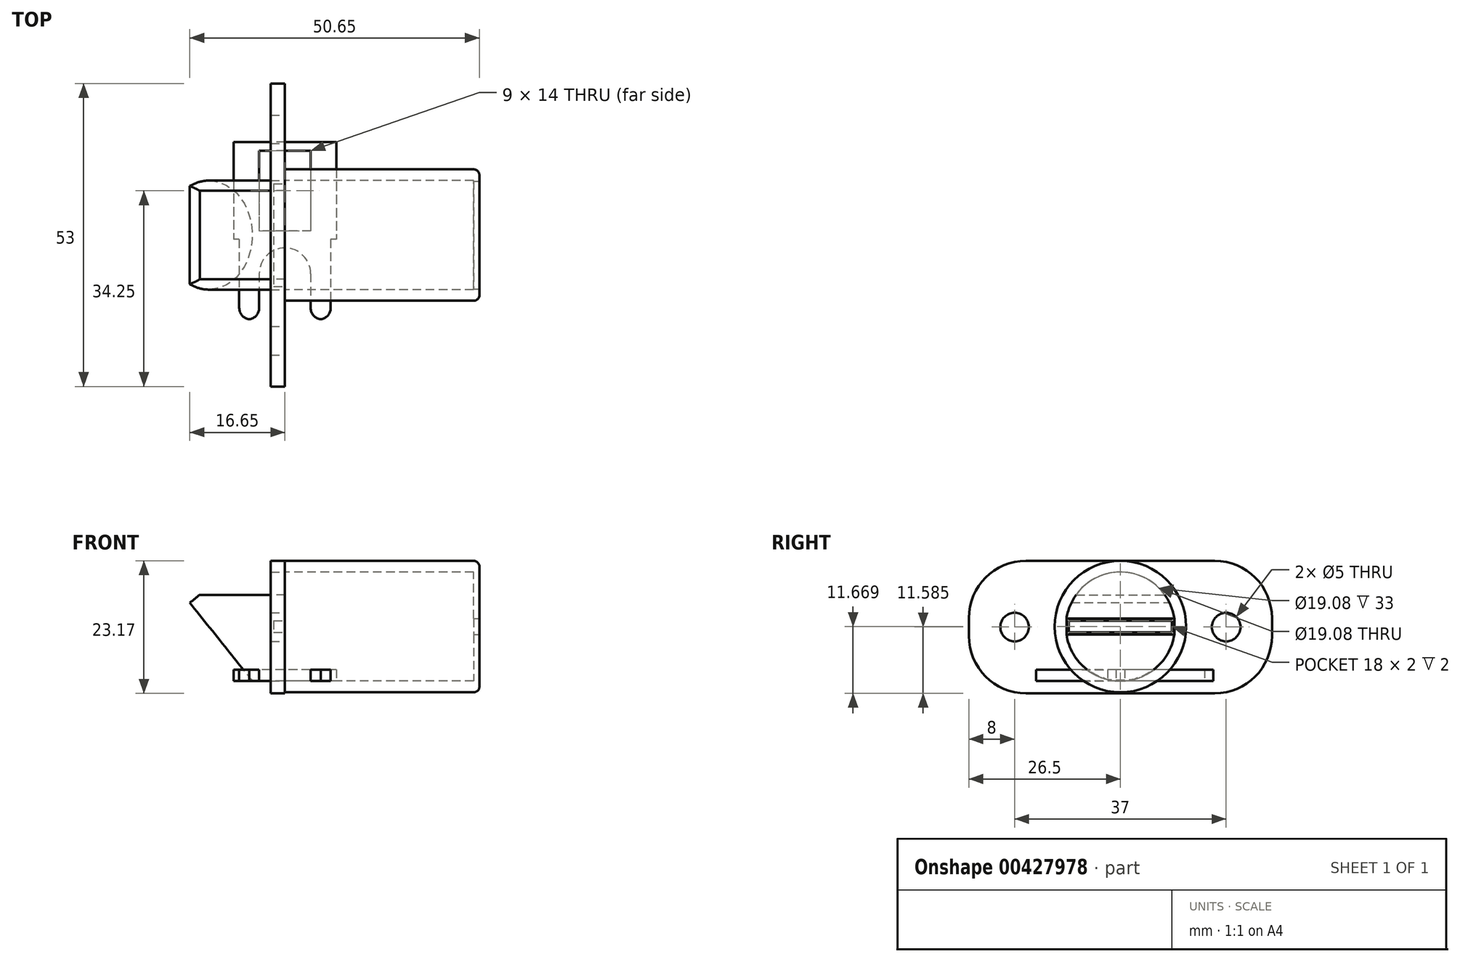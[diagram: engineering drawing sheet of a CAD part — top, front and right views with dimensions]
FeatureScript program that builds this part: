
annotation { "Feature Type Name" : "Feature", "Feature Type Description" : "" }
export const myFeature = defineFeature(function(context is Context, id is Id, definition is map)
    precondition{}
    {
        {
            var Q0;
            Q0=qCreatedBy(makeId("Front.planeOp"),FACE);
            var sketch = newSketch(context, id + "F0", { "sketchPlane" : qUnion([Q0])});
            skLineSegment(sketch, "E0", {"start": v(0, 0) * mm, "end": v(0, 15.1) * mm});
            skLineSegment(sketch, "E1", {"start": v(0, 15.1) * mm, "end": v(-14.9, 15.1) * mm});
            skLineSegment(sketch, "E2", {"start": v(0, 0) * mm, "end": v(-5.67, 0) * mm});
            skLineSegment(sketch, "E3", {"start": v(-5.67, 0) * mm, "end": v(-16.65, 13.71) * mm});
            skLineSegment(sketch, "E4", {"start": v(-16.65, 13.71) * mm, "end": v(-14.9, 15.1) * mm});
            skSolve(sketch);
        }
        {
            var Q0;
            Q0 = qSketchRegion(id + "F0", true);
            extrude(context, id + "F1", {"entities" : qUnion([Q0]), "depth" : 15.5 * mm});
        }
        {
            var Q0;
            Q0=makeQuery(id+"F1.opExtrude","SWEPT_FACE",FACE,{"disambiguationData":[OSD([sQuery(id+"F0.wireOp",EDGE,"E0")])]});
            var sketch = newSketch(context, id + "F2", { "sketchPlane" : qUnion([Q0])});
            skCircle(sketch, "E5", {"center": v(-7.75, 9.54) * mm, "radius": 9.54 * mm});
            skSolve(sketch);
        }
        {
            var Q0;
            {var subQ0=sQuery(id+"F2.wireOp",EDGE,"E5");var subQ1=sQuery(id+"F0.wireOp",EDGE,"E0");var subQ2=makeQuery(id+"F1.opExtrude","CAP_EDGE",EDGE,{"disambiguationData":[OSD([subQ1])],"isStart":false});var subQ4=makeQuery(id+"F2.imprint","INTERSECT",VERTEX,{"derivedFrom":[subQ2,subQ0]});Q0=makeQuery(id+"F2.imprint","IMPRINT",FACE,{"disambiguationData":[TD([[makeQuery(id+"F2.imprint","IMPRINT",EDGE,{"disambiguationData":[TD([[subQ4,1.0]])],"derivedFrom":subQ0}),1.0]])]});}
            var Q1;
            {var subQ0=sQuery(id+"F2.wireOp",EDGE,"E5");var subQ1=sQuery(id+"F0.wireOp",EDGE,"E0");var subQ2=makeQuery(id+"F1.opExtrude","CAP_EDGE",EDGE,{"disambiguationData":[OSD([subQ1])],"isStart":true});var subQ4=makeQuery(id+"F2.imprint","INTERSECT",VERTEX,{"derivedFrom":[subQ2,subQ0]});Q1=makeQuery(id+"F2.imprint","IMPRINT",FACE,{"disambiguationData":[TD([[makeQuery(id+"F2.imprint","IMPRINT",EDGE,{"disambiguationData":[TD([[subQ4,-1.0]])],"derivedFrom":subQ0}),1.0]])]});}
            extrude(context, id + "F3", {"entities" : qUnion([Q0, Q1]), "operationType" : NewBodyOperationType.ADD, "oppositeDirection" : true, "depth" : 16.67 * mm});
        }
        {
            var Q0;
            {var subQ0=sQuery(id+"F2.wireOp",EDGE,"E5");var subQ1=sQuery(id+"F0.wireOp",EDGE,"E0");var subQ2=makeQuery(id+"F1.opExtrude","CAP_EDGE",EDGE,{"disambiguationData":[OSD([subQ1])],"isStart":false});Q0=makeQuery(id+"F3.opExtrude","SWEPT_FACE",FACE,{"disambiguationData":[OSD([subQ1]),TDD([makeQuery(id+"F2.imprint","IMPRINT",EDGE,{"disambiguationData":[TD([[makeQuery(id+"F2.imprint","INTERSECT",VERTEX,{"derivedFrom":[subQ2,subQ0]}),-1.0]])],"derivedFrom":subQ2})])]});}
            extrude(context, id + "F4", {"entities" : qUnion([Q0]), "operationType" : NewBodyOperationType.REMOVE, "endBound" : BoundingType.THROUGH_ALL, "oppositeDirection" : true, "depth" : 25 * mm});
        }
        {
            var Q0;
            {var subQ0=sQuery(id+"F2.wireOp",EDGE,"E5");var subQ1=sQuery(id+"F0.wireOp",EDGE,"E0");var subQ2=makeQuery(id+"F1.opExtrude","CAP_EDGE",EDGE,{"disambiguationData":[OSD([subQ1])],"isStart":true});Q0=makeQuery(id+"F3.opExtrude","SWEPT_FACE",FACE,{"disambiguationData":[OSD([subQ1]),TDD([makeQuery(id+"F2.imprint","IMPRINT",EDGE,{"disambiguationData":[TD([[makeQuery(id+"F2.imprint","INTERSECT",VERTEX,{"derivedFrom":[subQ2,subQ0]}),-1.0]])],"derivedFrom":subQ2})])]});}
            extrude(context, id + "F5", {"entities" : qUnion([Q0]), "operationType" : NewBodyOperationType.REMOVE, "endBound" : BoundingType.THROUGH_ALL, "oppositeDirection" : true, "depth" : 25 * mm});
        }
        {
            var Q0;
            {var subQ0=sQuery(id+"F2.wireOp",EDGE,"E5");var subQ1=sQuery(id+"F0.wireOp",EDGE,"E0");var subQ2=makeQuery(id+"F1.opExtrude","CAP_EDGE",EDGE,{"disambiguationData":[OSD([subQ1])],"isStart":false});var subQ3=makeQuery(id+"F2.imprint","INTERSECT",VERTEX,{"derivedFrom":[subQ2,subQ0]});Q0=makeQuery(id+"F2.imprint","IMPRINT",FACE,{"disambiguationData":[TD([[makeQuery(id+"F2.imprint","IMPRINT",EDGE,{"disambiguationData":[TD([[subQ3,-1.0]])],"derivedFrom":subQ0}),-1.0]])]});}
            var Q1;
            {var subQ0=sQuery(id+"F2.wireOp",EDGE,"E5");var subQ1=sQuery(id+"F0.wireOp",EDGE,"E0");var subQ4=makeQuery(id+"F1.opExtrude","CAP_EDGE",EDGE,{"disambiguationData":[OSD([subQ1])],"isStart":true});var subQ5=makeQuery(id+"F2.imprint","INTERSECT",VERTEX,{"derivedFrom":[subQ4,subQ0]});Q1=makeQuery(id+"F2.imprint","IMPRINT",FACE,{"disambiguationData":[TD([[makeQuery(id+"F2.imprint","IMPRINT",EDGE,{"disambiguationData":[TD([[subQ5,1.0]])],"derivedFrom":subQ0}),-1.0]])]});}
            extrude(context, id + "F6", {"entities" : qUnion([Q0, Q1]), "operationType" : NewBodyOperationType.REMOVE, "endBound" : BoundingType.THROUGH_ALL, "oppositeDirection" : true, "depth" : 25 * mm});
        }
        {
            var Q0;
            {var subQ1=sQuery(id+"F0.wireOp",EDGE,"E0");var subQ3=makeQuery(id+"F1.opExtrude","SWEPT_EDGE",EDGE,{"disambiguationData":[OSD([subQ1,sQuery(id+"F0.wireOp",EDGE,"E1")])]});Q0=makeQuery(id+"F2.imprint","IMPRINT",FACE,{"disambiguationData":[TD([[makeQuery(id+"F2.imprint","IMPRINT",EDGE,{"derivedFrom":subQ3}),-1.0]])]});}
            var sketch = newSketch(context, id + "F7", { "sketchPlane" : qUnion([Q0])});
            skCircle(sketch, "E6", {"center": v(-7.75, 9.54) * mm, "radius": 11.5 * mm});
            skSolve(sketch);
        }
        {
            var Q0;
            Q0 = qSketchRegion(id + "F7", true);
            extrude(context, id + "F8", {"entities" : qUnion([Q0]), "depth" : 34 * mm});
        }
        {
            var Q0;
            {var subQ1=sQuery(id+"F0.wireOp",EDGE,"E0");var subQ2=makeQuery(id+"F1.opExtrude","SWEPT_EDGE",EDGE,{"disambiguationData":[OSD([subQ1,sQuery(id+"F0.wireOp",EDGE,"E1")])]});Q0=makeQuery(id+"F2.imprint","IMPRINT",FACE,{"disambiguationData":[TD([[makeQuery(id+"F2.imprint","IMPRINT",EDGE,{"derivedFrom":subQ2}),1.0]])]});}
            var Q1;
            {var subQ0=sQuery(id+"F2.wireOp",EDGE,"E5");var subQ1=sQuery(id+"F0.wireOp",EDGE,"E0");var subQ2=makeQuery(id+"F1.opExtrude","CAP_EDGE",EDGE,{"disambiguationData":[OSD([subQ1])],"isStart":false});var subQ4=makeQuery(id+"F2.imprint","INTERSECT",VERTEX,{"derivedFrom":[subQ2,subQ0]});Q1=makeQuery(id+"F2.imprint","IMPRINT",FACE,{"disambiguationData":[TD([[makeQuery(id+"F2.imprint","IMPRINT",EDGE,{"disambiguationData":[TD([[subQ4,1.0]])],"derivedFrom":subQ0}),1.0]])]});}
            var Q2;
            {var subQ1=sQuery(id+"F0.wireOp",EDGE,"E0");var subQ3=makeQuery(id+"F1.opExtrude","SWEPT_EDGE",EDGE,{"disambiguationData":[OSD([subQ1,sQuery(id+"F0.wireOp",EDGE,"E1")])]});Q2=makeQuery(id+"F2.imprint","IMPRINT",FACE,{"disambiguationData":[TD([[makeQuery(id+"F2.imprint","IMPRINT",EDGE,{"derivedFrom":subQ3}),-1.0]])]});}
            var Q3;
            {var subQ0=sQuery(id+"F2.wireOp",EDGE,"E5");var subQ1=sQuery(id+"F0.wireOp",EDGE,"E0");var subQ2=makeQuery(id+"F1.opExtrude","CAP_EDGE",EDGE,{"disambiguationData":[OSD([subQ1])],"isStart":true});var subQ4=makeQuery(id+"F2.imprint","INTERSECT",VERTEX,{"derivedFrom":[subQ2,subQ0]});Q3=makeQuery(id+"F2.imprint","IMPRINT",FACE,{"disambiguationData":[TD([[makeQuery(id+"F2.imprint","IMPRINT",EDGE,{"disambiguationData":[TD([[subQ4,-1.0]])],"derivedFrom":subQ0}),1.0]])]});}
            extrude(context, id + "F9", {"entities" : qUnion([Q0, Q1, Q2, Q3]), "operationType" : NewBodyOperationType.REMOVE, "depth" : 33 * mm});
        }
        {
            var Q0;
            Q0=makeQuery(id+"F8.opExtrude","CAP_FACE",FACE,{"disambiguationData":[OSD([sQuery(id+"F7.wireOp",EDGE,"E6")])],"isStart":true});
            var sketch = newSketch(context, id + "F10", { "sketchPlane" : qUnion([Q0])});
            skLineSegment(sketch, "E7.bottom", {"start": v(-18.75, 21.04) * mm, "end": v(34.25, 21.04) * mm});
            skLineSegment(sketch, "E7.top", {"start": v(-18.75, -2.13) * mm, "end": v(34.25, -2.13) * mm});
            skLineSegment(sketch, "E7.left", {"start": v(-18.75, 21.04) * mm, "end": v(-18.75, -2.13) * mm});
            skLineSegment(sketch, "E7.right", {"start": v(34.25, 21.04) * mm, "end": v(34.25, -2.13) * mm});
            skCircle(sketch, "E8", {"center": v(26.25, 9.45) * mm, "radius": 2.5 * mm});
            skPoint(sketch, "E8.centerSnap0", {"position": v(34.25, 9.45) * mm});
            skCircle(sketch, "E9", {"center": v(-10.75, 9.45) * mm, "radius": 2.5 * mm});
            skPoint(sketch, "E9.centerSnap0", {"position": v(-18.75, 9.45) * mm});
            skCircle(sketch, "E10", {"center": v(7.75, 9.54) * mm, "radius": 9.54 * mm});
            skSolve(sketch);
        }
        {
            var Q0;
            Q0=makeQuery(id+"F10.imprint","IMPRINT",FACE,{"disambiguationData":[TD([[makeQuery(id+"F10.imprint","IMPRINT",EDGE,{"derivedFrom":sQuery(id+"F10.wireOp",EDGE,"E10")}),1.0]])]});
            var Q1;
            Q1=makeQuery(id+"F10.imprint","IMPRINT",FACE,{"disambiguationData":[TD([[makeQuery(id+"F10.imprint","IMPRINT",EDGE,{"derivedFrom":sQuery(id+"F10.wireOp",EDGE,"E7.top")}),1.0]])]});
            extrude(context, id + "F11", {"entities" : qUnion([Q0, Q1]), "depth" : 2.5 * mm});
        }
        {
            var Q0;
            Q0=makeQuery(id+"F11.opExtrude","SWEPT_EDGE",EDGE,{"disambiguationData":[OSD([sQuery(id+"F10.wireOp",EDGE,"E7.bottom"),sQuery(id+"F10.wireOp",EDGE,"E7.left")])]});
            var Q1;
            Q1=makeQuery(id+"F11.opExtrude","SWEPT_EDGE",EDGE,{"disambiguationData":[OSD([sQuery(id+"F10.wireOp",EDGE,"E7.bottom"),sQuery(id+"F10.wireOp",EDGE,"E7.right")])]});
            var Q2;
            Q2=makeQuery(id+"F11.opExtrude","SWEPT_EDGE",EDGE,{"disambiguationData":[OSD([sQuery(id+"F10.wireOp",EDGE,"E7.top"),sQuery(id+"F10.wireOp",EDGE,"E7.right")])]});
            var Q3;
            Q3=makeQuery(id+"F11.opExtrude","SWEPT_EDGE",EDGE,{"disambiguationData":[OSD([sQuery(id+"F10.wireOp",EDGE,"E7.top"),sQuery(id+"F10.wireOp",EDGE,"E7.left")])]});
            fillet(context, id + "F12", {"entities" : qUnion([Q0, Q1, Q2, Q3]), "radius" : 10 * mm, "tangentPropagation" : true, "allowEdgeOverflow" : false});
        }
        {
            var Q0;
            Q0=makeQuery(id+"F8.opExtrude","CAP_EDGE",EDGE,{"disambiguationData":[OSD([sQuery(id+"F7.wireOp",EDGE,"E6")])],"isStart":false});
            fillet(context, id + "F13", {"entities" : qUnion([Q0]), "radius" : 1 * mm, "tangentPropagation" : true, "allowEdgeOverflow" : false});
        }
        {
            var Q0;
            Q0=makeQuery(id+"F8.opExtrude","CAP_FACE",FACE,{"disambiguationData":[OSD([sQuery(id+"F7.wireOp",EDGE,"E6")])],"isStart":false});
            var sketch = newSketch(context, id + "F14", { "sketchPlane" : qUnion([Q0])});
            skLineSegment(sketch, "E11.bottom", {"start": v(-17.18, 10.94) * mm, "end": v(1.68, 10.94) * mm});
            skLineSegment(sketch, "E11.top", {"start": v(-17.18, 8.13) * mm, "end": v(1.68, 8.13) * mm});
            skLineSegment(sketch, "E11.left", {"start": v(-17.18, 10.94) * mm, "end": v(-17.18, 8.13) * mm});
            skLineSegment(sketch, "E11.right", {"start": v(1.68, 10.94) * mm, "end": v(1.68, 8.13) * mm});
            skSolve(sketch);
        }
        {
            var Q0;
            Q0 = qSketchRegion(id + "F14", true);
            extrude(context, id + "F15", {"entities" : qUnion([Q0]), "operationType" : NewBodyOperationType.REMOVE, "oppositeDirection" : true, "depth" : 3 * mm});
        }
        {
            var Q0;
            Q0=makeQuery(id+"F15.boolean.opBoolean","COPY",FACE,{"derivedFrom":makeQuery(id+"F15.opExtrude","SWEPT_FACE",FACE,{"disambiguationData":[OSD([sQuery(id+"F14.wireOp",EDGE,"E11.top")])]})});
            var sketch = newSketch(context, id + "F16", { "sketchPlane" : qUnion([Q0])});
            skLineSegment(sketch, "E12.bottom", {"start": v(29.79, 0) * mm, "end": v(59.79, 0) * mm});
            skLineSegment(sketch, "E12.top", {"start": v(29.79, -18) * mm, "end": v(59.79, -18) * mm});
            skLineSegment(sketch, "E12.left", {"start": v(29.79, 0) * mm, "end": v(29.79, -18) * mm});
            skLineSegment(sketch, "E12.right", {"start": v(59.79, 0) * mm, "end": v(59.79, -18) * mm});
            skCircle(sketch, "E13", {"center": v(44.79, -9) * mm, "radius": 5.2 * mm});
            skSolve(sketch);
        }
        {
            var Q0;
            Q0=makeQuery(id+"F16.imprint","IMPRINT",FACE,{"disambiguationData":[TD([[makeQuery(id+"F16.imprint","IMPRINT",EDGE,{"derivedFrom":sQuery(id+"F16.wireOp",EDGE,"E12.top")}),1.0]])]});
            var Q1;
            {var subQ1=sQuery(id+"F14.wireOp",EDGE,"E11.top");var subQ6=makeQuery(id+"F15.boolean.opBoolean","COPY",EDGE,{"derivedFrom":makeQuery(id+"F15.opExtrude","SWEPT_EDGE",EDGE,{"disambiguationData":[OSD([subQ1,sQuery(id+"F14.wireOp",EDGE,"E11.left")])]})});Q1=makeQuery(id+"F16.imprint","IMPRINT",FACE,{"disambiguationData":[TD([[makeQuery(id+"F16.imprint","IMPRINT",EDGE,{"derivedFrom":subQ6}),1.0]])]});}
            extrude(context, id + "F17", {"entities" : qUnion([Q0, Q1]), "depth" : 2.9 * mm});
        }
        {
            var Q0;
            Q0=makeQuery(id+"F17.opExtrude","SWEPT_EDGE",EDGE,{"disambiguationData":[OSD([sQuery(id+"F16.wireOp",EDGE,"E12.bottom"),sQuery(id+"F16.wireOp",EDGE,"E12.right")])]});
            var Q1;
            Q1=makeQuery(id+"F17.opExtrude","SWEPT_EDGE",EDGE,{"disambiguationData":[OSD([sQuery(id+"F16.wireOp",EDGE,"E12.top"),sQuery(id+"F16.wireOp",EDGE,"E12.right")])]});
            fillet(context, id + "F18", {"entities" : qUnion([Q0, Q1]), "radius" : 5 * mm, "tangentPropagation" : true, "allowEdgeOverflow" : false});
        }
        {
            var Q0;
            Q0=qCreatedBy(makeId("Top.planeOp"),FACE);
            var sketch = newSketch(context, id + "F19", { "sketchPlane" : qUnion([Q0])});
            skLineSegment(sketch, "E14.bottom", {"start": v(9, 8.5) * mm, "end": v(-9, 8.5) * mm});
            skLineSegment(sketch, "E14.top", {"start": v(9, -8.5) * mm, "end": v(-9, -8.5) * mm});
            skLineSegment(sketch, "E14.left", {"start": v(9, 8.5) * mm, "end": v(9, -8.5) * mm});
            skLineSegment(sketch, "E14.right", {"start": v(-9, 8.5) * mm, "end": v(-9, -8.5) * mm});
            skPoint(sketch, "E14.middle", {"position": v(0, 0) * mm});
            skLineSegment(sketch, "E15.bottom", {"start": v(4.5, 7) * mm, "end": v(-4.5, 7) * mm});
            skLineSegment(sketch, "E15.top", {"start": v(4.5, -7) * mm, "end": v(-4.5, -7) * mm});
            skLineSegment(sketch, "E15.left", {"start": v(4.5, 7) * mm, "end": v(4.5, -7) * mm});
            skLineSegment(sketch, "E15.right", {"start": v(-4.5, 7) * mm, "end": v(-4.5, -7) * mm});
            skLineSegment(sketch, "E16.bottom", {"start": v(-8, -8.5) * mm, "end": v(8, -8.5) * mm});
            skLineSegment(sketch, "E16.top", {"start": v(-8, -22.5) * mm, "end": v(-4.5, -22.5) * mm});
            skLineSegment(sketch, "E16.left", {"start": v(-8, -8.5) * mm, "end": v(-8, -22.5) * mm});
            skLineSegment(sketch, "E16.right", {"start": v(8, -8.5) * mm, "end": v(8, -22.5) * mm});
            skArc(sketch, "E17", {"start": v(4.5, -14.5) * mm, "mid": v(0, -10) * mm, "end": v(-4.5, -14.5) * mm});
            skLineSegment(sketch, "E18", {"start": v(-4.5, -14.5) * mm, "end": v(-4.5, -22.5) * mm});
            skLineSegment(sketch, "E19", {"start": v(4.5, -14.5) * mm, "end": v(4.5, -22.5) * mm});
            skLineSegment(sketch, "E20.trimOffspring", {"start": v(4.5, -22.5) * mm, "end": v(8, -22.5) * mm});
            skSolve(sketch);
        }
        {
            var Q0;
            Q0 = qSketchRegion(id + "F19", true);
            extrude(context, id + "F20", {"entities" : qUnion([Q0]), "depth" : 2 * mm});
        }
        {
            var Q0;
            Q0=makeQuery(id+"F20.opExtrude","SWEPT_EDGE",EDGE,{"disambiguationData":[OSD([sQuery(id+"F19.wireOp",EDGE,"E16.top"),sQuery(id+"F19.wireOp",EDGE,"E18")])]});
            var Q1;
            Q1=makeQuery(id+"F20.opExtrude","SWEPT_EDGE",EDGE,{"disambiguationData":[OSD([sQuery(id+"F19.wireOp",EDGE,"E16.top"),sQuery(id+"F19.wireOp",EDGE,"E16.left")])]});
            var Q2;
            Q2=makeQuery(id+"F20.opExtrude","SWEPT_EDGE",EDGE,{"disambiguationData":[OSD([sQuery(id+"F19.wireOp",EDGE,"E16.right"),sQuery(id+"F19.wireOp",EDGE,"E20.trimOffspring")])]});
            var Q3;
            Q3=makeQuery(id+"F20.opExtrude","SWEPT_EDGE",EDGE,{"disambiguationData":[OSD([sQuery(id+"F19.wireOp",EDGE,"E19"),sQuery(id+"F19.wireOp",EDGE,"E20.trimOffspring")])]});
            fillet(context, id + "F21", {"entities" : qUnion([Q0, Q1, Q2, Q3]), "radius" : 2 * mm, "tangentPropagation" : true, "allowEdgeOverflow" : false});
        }
        {
            var Q0;
            Q0=makeQuery(id+"F17.opExtrude","SWEPT_BODY",BODY,{"disambiguationData":[OSD([sQuery(id+"F16.wireOp",EDGE,"E12.bottom"),sQuery(id+"F16.wireOp",EDGE,"E12.top"),sQuery(id+"F16.wireOp",EDGE,"E12.left"),sQuery(id+"F16.wireOp",EDGE,"E12.right"),sQuery(id+"F16.wireOp",EDGE,"E13")])]});
            deleteBodies(context, id + "F22", {"entities" : qUnion([Q0])});
        }
        {
            var Q0;
            {var subQ0=sQuery(id+"F2.wireOp",EDGE,"E5");var subQ1=sQuery(id+"F0.wireOp",EDGE,"E0");var subQ2=makeQuery(id+"F1.opExtrude","CAP_EDGE",EDGE,{"disambiguationData":[OSD([subQ1])],"isStart":true});var subQ5=makeQuery(id+"F2.imprint","INTERSECT",VERTEX,{"derivedFrom":[subQ2,subQ0]});var subQ6=makeQuery(id+"F1.opExtrude","CAP_EDGE",EDGE,{"disambiguationData":[OSD([subQ1])],"isStart":false});var subQ8=makeQuery(id+"F2.imprint","INTERSECT",VERTEX,{"derivedFrom":[subQ6,subQ0]});Q0=makeQuery(id+"F3.boolean.opBoolean","MERGE",FACE,{"derivedFrom":[makeQuery(id+"F1.opExtrude","SWEPT_FACE",FACE,{"disambiguationData":[OSD([subQ1])]}),makeQuery(id+"F3.opExtrude","CAP_FACE",FACE,{"disambiguationData":[OSD([subQ1,subQ0]),TDD([makeQuery(id+"F2.imprint","IMPRINT",EDGE,{"disambiguationData":[TD([[subQ8,1.0]])],"derivedFrom":subQ0}),makeQuery(id+"F2.imprint","IMPRINT",EDGE,{"disambiguationData":[TD([[subQ8,-1.0]])],"derivedFrom":subQ6})])],"isStart":true}),makeQuery(id+"F3.opExtrude","CAP_FACE",FACE,{"disambiguationData":[OSD([subQ1,subQ0]),TDD([makeQuery(id+"F2.imprint","IMPRINT",EDGE,{"disambiguationData":[TD([[subQ5,-1.0]])],"derivedFrom":subQ0}),makeQuery(id+"F2.imprint","IMPRINT",EDGE,{"disambiguationData":[TD([[subQ5,-1.0]])],"derivedFrom":subQ2})])],"isStart":true})]});}
            var sketch = newSketch(context, id + "F23", { "sketchPlane" : qUnion([Q0])});
            skLineSegment(sketch, "E21.bottom", {"start": v(1.25, 10.54) * mm, "end": v(-16.75, 10.54) * mm});
            skLineSegment(sketch, "E21.top", {"start": v(1.25, 8.54) * mm, "end": v(-16.75, 8.54) * mm});
            skLineSegment(sketch, "E21.left", {"start": v(1.25, 10.54) * mm, "end": v(1.25, 8.54) * mm});
            skLineSegment(sketch, "E21.right", {"start": v(-16.75, 10.54) * mm, "end": v(-16.75, 8.54) * mm});
            skPoint(sketch, "E21.middle", {"position": v(-7.75, 9.54) * mm});
            skSolve(sketch);
        }
        {
            var Q0;
            Q0 = qSketchRegion(id + "F23", true);
            extrude(context, id + "F24", {"entities" : qUnion([Q0]), "operationType" : NewBodyOperationType.REMOVE, "oppositeDirection" : true, "depth" : 2 * mm});
        }
    });
